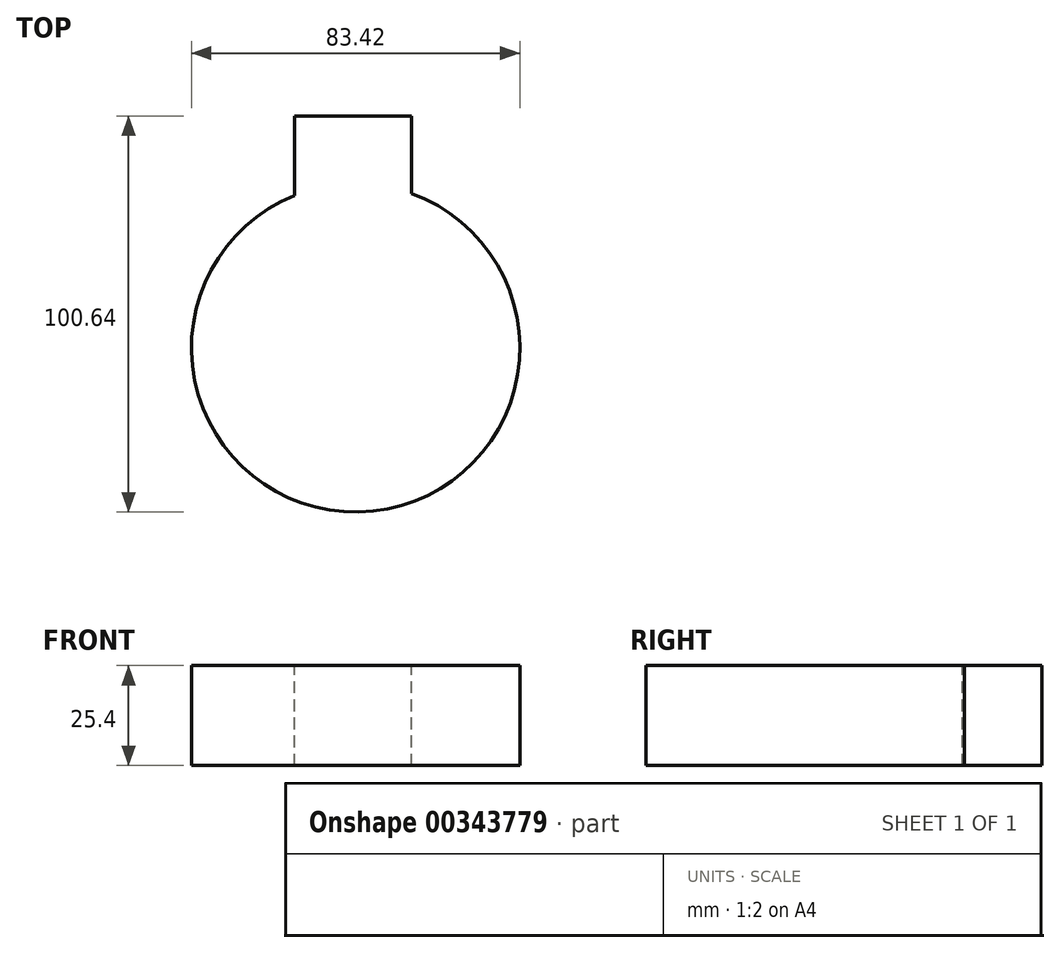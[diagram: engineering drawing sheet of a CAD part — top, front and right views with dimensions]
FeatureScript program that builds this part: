
annotation { "Feature Type Name" : "Feature", "Feature Type Description" : "" }
export const myFeature = defineFeature(function(context is Context, id is Id, definition is map)
    precondition{}
    {
        {
            var Q0;
            Q0=qCreatedBy(makeId("Top.planeOp"),FACE);
            var sketch = newSketch(context, id + "F0", { "sketchPlane" : qUnion([Q0])});
            skArc(sketch, "E0", {"start": v(-15.52, 38.72) * mm, "mid": v(0.74, -41.7) * mm, "end": v(14.14, 39.24) * mm});
            skLineSegment(sketch, "E1", {"start": v(-15.52, 38.72) * mm, "end": v(-15.52, 58.93) * mm});
            skLineSegment(sketch, "E2", {"start": v(-15.52, 58.93) * mm, "end": v(14.14, 58.93) * mm});
            skLineSegment(sketch, "E3", {"start": v(14.14, 58.93) * mm, "end": v(14.14, 39.24) * mm});
            skLineSegment(sketch, "E4", {"start": v(-26.93, 31.85) * mm, "end": v(39.23, -14.19) * mm});
            skSolve(sketch);
        }
        {
            var Q0;
            {var subQ0=sQuery(id+"F0.wireOp",EDGE,"E1");Q0=makeQuery(id+"F0.imprint","IMPRINT",FACE,{"disambiguationData":[TD([[makeQuery(id+"F0.imprint","IMPRINT",EDGE,{"derivedFrom":subQ0}),-1.0]])]});}
            var Q1;
            {var subQ0=sQuery(id+"F0.wireOp",EDGE,"E4");Q1=makeQuery(id+"F0.imprint","IMPRINT",FACE,{"disambiguationData":[TD([[makeQuery(id+"F0.imprint","IMPRINT",EDGE,{"derivedFrom":subQ0}),-1.0]])]});}
            extrude(context, id + "F1", {"entities" : qUnion([Q0, Q1]), "endBound" : BoundingType.SYMMETRIC, "oppositeDirection" : true, "depth" : 25.4 * mm, "offsetDistance" : 25.4 * mm});
        }
    });
